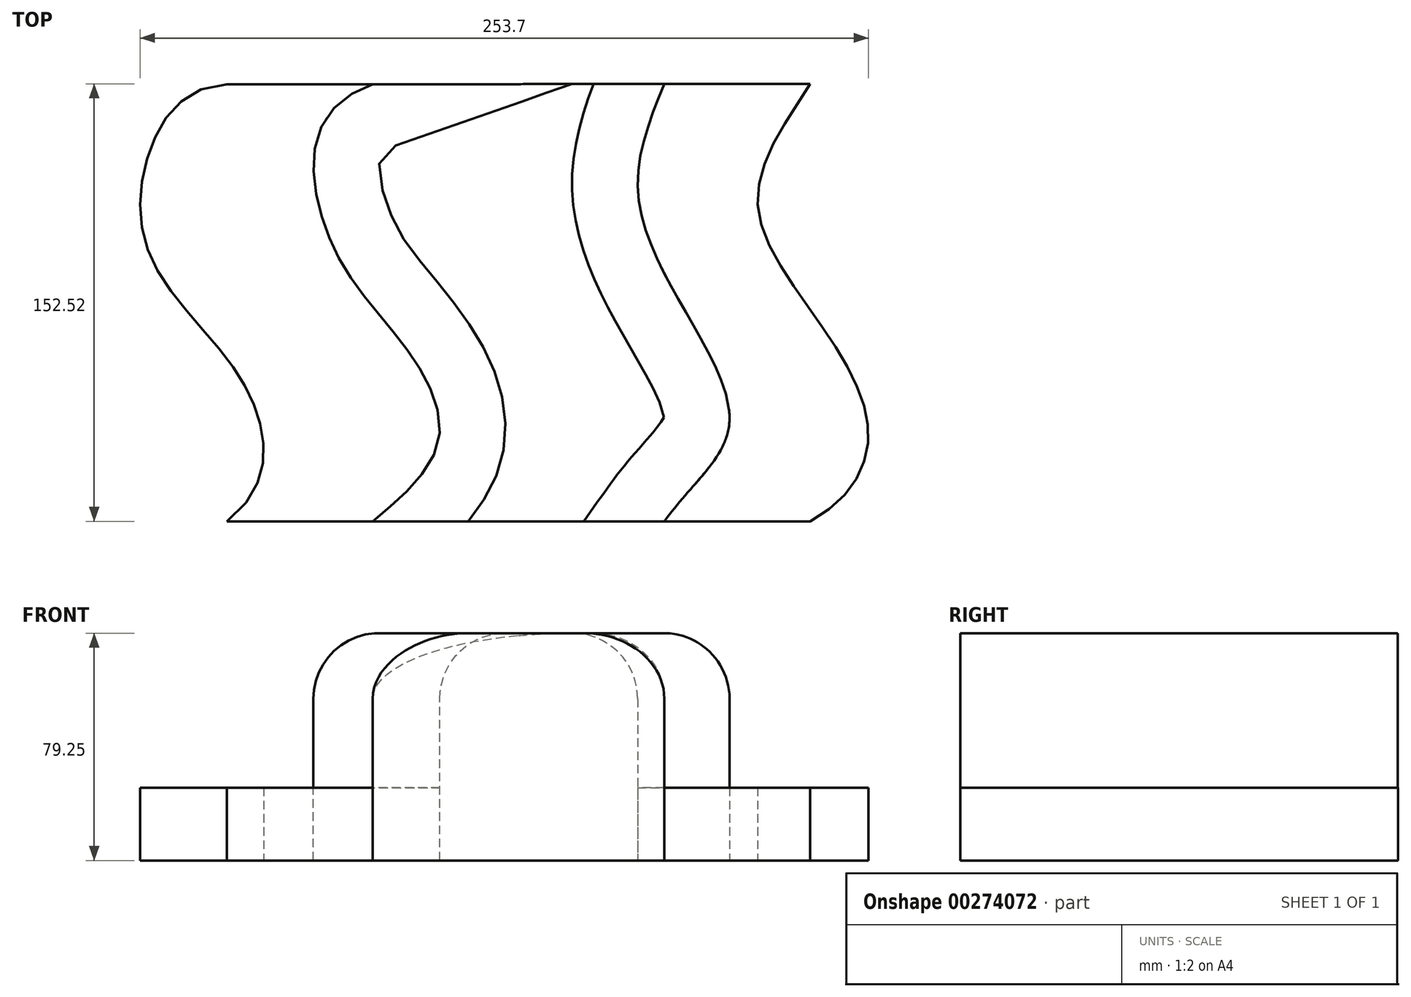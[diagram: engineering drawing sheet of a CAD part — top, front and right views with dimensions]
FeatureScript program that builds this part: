
annotation { "Feature Type Name" : "Feature", "Feature Type Description" : "" }
export const myFeature = defineFeature(function(context is Context, id is Id, definition is map)
    precondition{}
    {
        {
            var Q0;
            Q0=qCreatedBy(makeId("Top.planeOp"),FACE);
            var sketch = newSketch(context, id + "F0", { "sketchPlane" : qUnion([Q0])});
            skLineSegment(sketch, "E0", {"start": v(0, 0) * mm, "end": v(0, 76.2) * mm});
            skLineSegment(sketch, "E1", {"start": v(0, 0) * mm, "end": v(0, -76.2) * mm});
            skLineSegment(sketch, "E2", {"start": v(0, 76.2) * mm, "end": v(-101.6, 76.2) * mm});
            skLineSegment(sketch, "E3", {"start": v(0, 76.2) * mm, "end": v(101.6, 76.32) * mm});
            skLineSegment(sketch, "E4", {"start": v(0, -76.2) * mm, "end": v(-101.6, -76.2) * mm});
            skLineSegment(sketch, "E5", {"start": v(0, -76.2) * mm, "end": v(101.6, -76.2) * mm});
            skFitSpline(sketch, "E6", {"points": [v(-101.6, 76.2) * mm, v(-128.3, 53.4) * mm, v(-128.56, 16.75) * mm, v(-102.95, -17.75) * mm, v(-89.2, -46.32) * mm, v(-101.6, -76.2) * mm], "startDerivative": vector(-232.27, -15.04) * mm, "endDerivative": vector(-187.24, -146.33) * mm});
            skFitSpline(sketch, "E7", {"points": [v(101.6, -76.2) * mm, v(121.85, -47.67) * mm, v(106.48, -9.4) * mm, v(83.3, 34.8) * mm, v(101.6, 76.32) * mm], "startDerivative": vector(167.64, 88.64) * mm, "endDerivative": vector(101.67, 160.8) * mm});
            skPoint(sketch, "E8", {"position": v(-50.8, 76.2) * mm});
            skPoint(sketch, "E9", {"position": v(-50.8, -76.2) * mm});
            skPoint(sketch, "E10", {"position": v(50.8, 76.26) * mm});
            skPoint(sketch, "E11", {"position": v(50.8, -76.2) * mm});
            skFitSpline(sketch, "E12", {"points": [v(-50.8, 76.2) * mm, v(-70.07, 58) * mm, v(-62.8, 15.94) * mm, v(-38, -17.48) * mm, v(-27.75, -47.4) * mm, v(-50.8, -76.2) * mm], "startDerivative": vector(-154.9, -54.08) * mm, "endDerivative": vector(-168.67, -136.8) * mm});
            skFitSpline(sketch, "E13", {"points": [v(50.8, 76.26) * mm, v(41.52, 40.2) * mm, v(56.35, 0) * mm, v(73.33, -43.09) * mm, v(50.8, -76.2) * mm], "startDerivative": vector(-61.69, -149.4) * mm, "endDerivative": vector(-109.85, -153.7) * mm});
            skSolve(sketch);
        }
        {
            var Q0;
            {var subQ0=sQuery(id+"F0.wireOp",EDGE,"E6");Q0=makeQuery(id+"F0.imprint","IMPRINT",FACE,{"disambiguationData":[TD([[makeQuery(id+"F0.imprint","IMPRINT",EDGE,{"derivedFrom":subQ0}),1.0]])]});}
            extrude(context, id + "F1", {"entities" : qUnion([Q0]), "depth" : 25.4 * mm});
        }
        {
            var Q0;
            {var subQ0=sQuery(id+"F0.wireOp",EDGE,"E7");Q0=makeQuery(id+"F0.imprint","IMPRINT",FACE,{"disambiguationData":[TD([[makeQuery(id+"F0.imprint","IMPRINT",EDGE,{"derivedFrom":subQ0}),1.0]])]});}
            extrude(context, id + "F2", {"entities" : qUnion([Q0]), "depth" : 25.4 * mm});
        }
        {
            var Q0;
            {var subQ4=sQuery(id+"F0.wireOp",EDGE,"E0");Q0=makeQuery(id+"F0.imprint","IMPRINT",FACE,{"disambiguationData":[TD([[makeQuery(id+"F0.imprint","IMPRINT",EDGE,{"derivedFrom":subQ4}),1.0]])]});}
            var Q1;
            {var subQ4=sQuery(id+"F0.wireOp",EDGE,"E0");Q1=makeQuery(id+"F0.imprint","IMPRINT",FACE,{"disambiguationData":[TD([[makeQuery(id+"F0.imprint","IMPRINT",EDGE,{"derivedFrom":subQ4}),-1.0]])]});}
            extrude(context, id + "F3", {"entities" : qUnion([Q0, Q1]), "depth" : 79.25 * mm});
        }
        {
            var Q0;
            Q0=makeQuery(id+"F3.opExtrude","CAP_EDGE",EDGE,{"disambiguationData":[OSD([sQuery(id+"F0.wireOp",EDGE,"E12")])],"isStart":false});
            fillet(context, id + "F4", {"entities" : qUnion([Q0]), "radius" : 22.86 * mm, "tangentPropagation" : true, "allowEdgeOverflow" : false});
        }
        {
            var Q0;
            Q0=makeQuery(id+"F3.opExtrude","CAP_EDGE",EDGE,{"disambiguationData":[OSD([sQuery(id+"F0.wireOp",EDGE,"E13")])],"isStart":false});
            fillet(context, id + "F5", {"entities" : qUnion([Q0]), "radius" : 22.86 * mm, "tangentPropagation" : true, "allowEdgeOverflow" : false});
        }
    });
